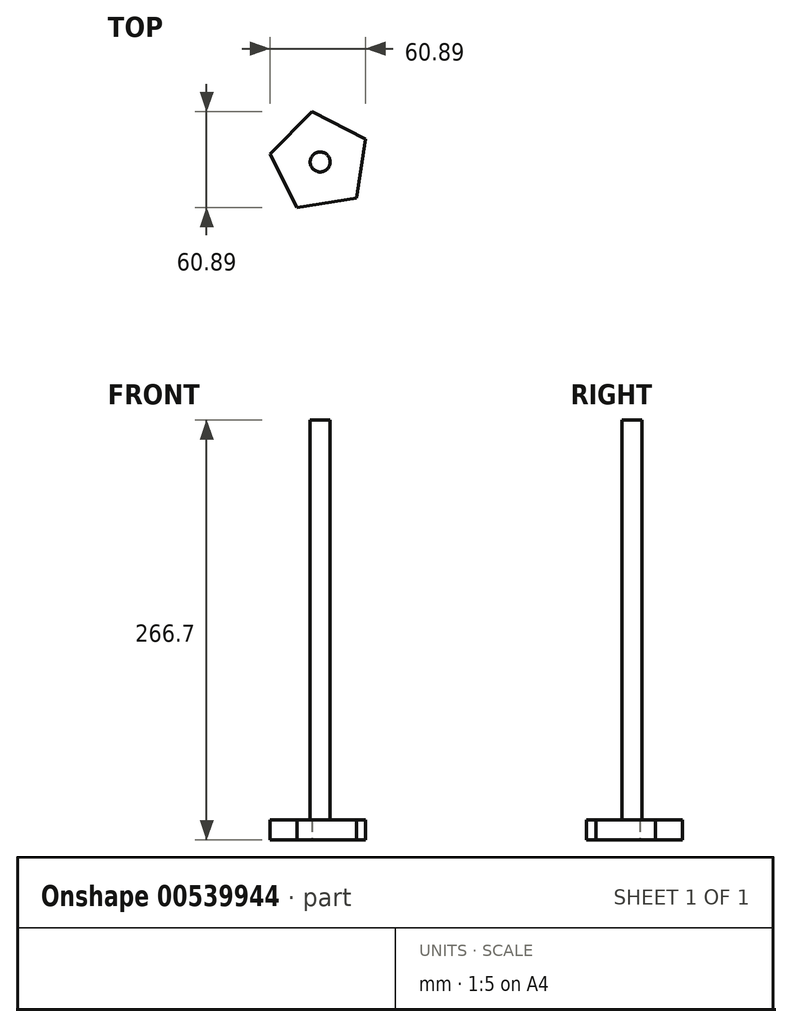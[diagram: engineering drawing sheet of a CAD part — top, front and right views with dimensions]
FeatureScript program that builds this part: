
annotation { "Feature Type Name" : "Feature", "Feature Type Description" : "" }
export const myFeature = defineFeature(function(context is Context, id is Id, definition is map)
    precondition{}
    {
        {
            var Q0;
            Q0=qCreatedBy(makeId("Top.planeOp"),FACE);
            var sketch = newSketch(context, id + "F0", { "sketchPlane" : qUnion([Q0])});
            skCircle(sketch, "E0.cCircle", {"center": v(0, 0) * mm, "radius": 32.4 * mm, "construction": true});
            skLineSegment(sketch, "E0.0", {"start": v(22.92, -22.92) * mm, "end": v(-14.71, -28.88) * mm});
            skLineSegment(sketch, "E0.1", {"start": v(-14.71, -28.88) * mm, "end": v(-32.01, 5.07) * mm});
            skLineSegment(sketch, "E0.2", {"start": v(-32.01, 5.07) * mm, "end": v(-5.07, 32.01) * mm});
            skLineSegment(sketch, "E0.3", {"start": v(-5.07, 32.01) * mm, "end": v(28.88, 14.71) * mm});
            skLineSegment(sketch, "E0.4", {"start": v(28.88, 14.71) * mm, "end": v(22.92, -22.92) * mm});
            skSolve(sketch);
        }
        {
            var Q0;
            Q0 = qSketchRegion(id + "F0", true);
            extrude(context, id + "F1", {"entities" : qUnion([Q0]), "depth" : 12.7 * mm, "offsetDistance" : 25.4 * mm});
        }
        {
            var Q0;
            Q0=makeQuery(id+"F1.opExtrude","CAP_FACE",FACE,{"disambiguationData":[OSD([sQuery(id+"F0.wireOp",EDGE,"E0.0"),sQuery(id+"F0.wireOp",EDGE,"E0.1"),sQuery(id+"F0.wireOp",EDGE,"E0.2"),sQuery(id+"F0.wireOp",EDGE,"E0.3"),sQuery(id+"F0.wireOp",EDGE,"E0.4")])],"isStart":false});
            var sketch = newSketch(context, id + "F2", { "sketchPlane" : qUnion([Q0])});
            skCircle(sketch, "E1", {"center": v(0, 0) * mm, "radius": 6.35 * mm});
            skSolve(sketch);
        }
        {
            var Q0;
            Q0=makeQuery(id+"F2.imprint","IMPRINT",FACE,{"disambiguationData":[TD([[makeQuery(id+"F2.imprint","IMPRINT",EDGE,{"derivedFrom":sQuery(id+"F2.wireOp",EDGE,"E1")}),1.0]])]});
            extrude(context, id + "F3", {"entities" : qUnion([Q0]), "operationType" : NewBodyOperationType.ADD, "depth" : 254 * mm, "offsetDistance" : 25.4 * mm});
        }
    });
